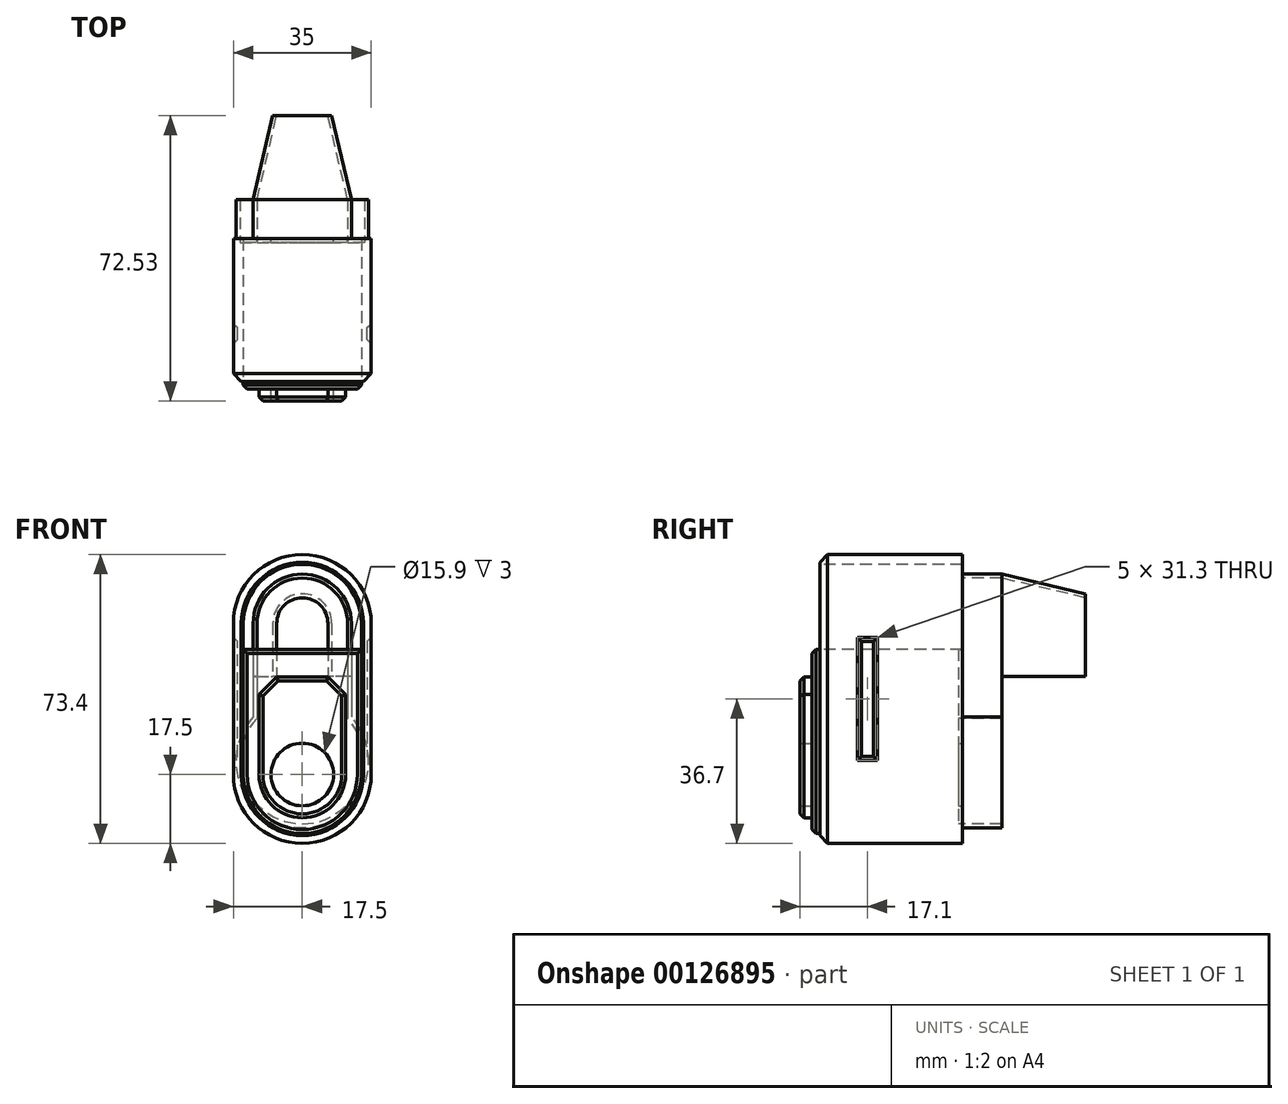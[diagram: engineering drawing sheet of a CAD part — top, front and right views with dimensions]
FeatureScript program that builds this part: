
annotation { "Feature Type Name" : "Feature", "Feature Type Description" : "" }
export const myFeature = defineFeature(function(context is Context, id is Id, definition is map)
    precondition{}
    {
        {
            var Q0;
            Q0=qCreatedBy(makeId("Front.planeOp"),FACE);
            var sketch = newSketch(context, id + "F0", { "sketchPlane" : qUnion([Q0])});
            skArc(sketch, "E0", {"start": v(-7.95, 0) * mm, "mid": v(-5.62, -5.62) * mm, "end": v(0, -7.95) * mm});
            skArc(sketch, "E1", {"start": v(-11, 0) * mm, "mid": v(0, -11) * mm, "end": v(11, 0) * mm});
            skArc(sketch, "E2", {"start": v(-15, 0) * mm, "mid": v(0, -15) * mm, "end": v(15, 0) * mm});
            skArc(sketch, "E3", {"start": v(-17.5, 0) * mm, "mid": v(0, -17.5) * mm, "end": v(17.5, 0) * mm});
            skLineSegment(sketch, "E4", {"start": v(0, -17.5) * mm, "end": v(0, 55.9) * mm, "construction": true});
            skLineSegment(sketch, "E5", {"start": v(-17.5, 0) * mm, "end": v(17.5, 0) * mm, "construction": true});
            skLineSegment(sketch, "E6", {"start": v(-17.5, -17.5) * mm, "end": v(-17.5, 55.9) * mm, "construction": true});
            skLineSegment(sketch, "E7", {"start": v(17.5, 55.9) * mm, "end": v(17.5, -17.5) * mm, "construction": true});
            skLineSegment(sketch, "E8", {"start": v(-17.5, -17.5) * mm, "end": v(17.5, -17.5) * mm, "construction": true});
            skLineSegment(sketch, "E9", {"start": v(-17.5, 55.9) * mm, "end": v(17.5, 55.9) * mm, "construction": true});
            skPoint(sketch, "E10.orphan", {"position": v(0, -30.99) * mm});
            skLineSegment(sketch, "E11", {"start": v(-17.5, 19.2) * mm, "end": v(17.5, 19.2) * mm, "construction": true});
            skArc(sketch, "E12.MirrorCS", {"start": v(7.95, 0) * mm, "mid": v(5.62, -5.62) * mm, "end": v(0, -7.95) * mm});
            skArc(sketch, "E13.MirrorCS", {"start": v(-15, 38.4) * mm, "mid": v(0, 53.4) * mm, "end": v(15, 38.4) * mm});
            skArc(sketch, "E14.MirrorCS", {"start": v(-17.5, 38.4) * mm, "mid": v(0, 55.9) * mm, "end": v(17.5, 38.4) * mm});
            skLineSegment(sketch, "E15", {"start": v(-17.5, 38.4) * mm, "end": v(-17.5, 0) * mm});
            skLineSegment(sketch, "E16", {"start": v(17.5, 38.4) * mm, "end": v(17.5, 0) * mm});
            skLineSegment(sketch, "E17", {"start": v(-15, 38.4) * mm, "end": v(-15, 0) * mm});
            skLineSegment(sketch, "E18", {"start": v(15, 38.4) * mm, "end": v(15, 0) * mm});
            skArc(sketch, "E19.MirrorCS", {"start": v(-7.95, 0) * mm, "mid": v(-5.62, 5.62) * mm, "end": v(0, 7.95) * mm});
            skArc(sketch, "E20.MirrorCS", {"start": v(7.95, 0) * mm, "mid": v(5.62, 5.62) * mm, "end": v(0, 7.95) * mm});
            skLineSegment(sketch, "E21", {"start": v(-17.5, 24.8) * mm, "end": v(17.5, 24.8) * mm, "construction": true});
            skLineSegment(sketch, "E22", {"start": v(-17.5, 31.8) * mm, "end": v(17.5, 31.8) * mm, "construction": true});
            skLineSegment(sketch, "E23", {"start": v(-11, 0) * mm, "end": v(-11, 24.8) * mm});
            skLineSegment(sketch, "E24", {"start": v(11, 0) * mm, "end": v(11, 24.8) * mm});
            skLineSegment(sketch, "E25", {"start": v(11, 24.8) * mm, "end": v(-11, 24.8) * mm});
            skLineSegment(sketch, "E26", {"start": v(-15, 31.8) * mm, "end": v(15, 31.8) * mm});
            skSolve(sketch);
        }
        {
            var Q0;
            Q0 = qSketchRegion(id + "F0", true);
            var Q1;
            Q1=makeQuery(id+"F0.imprint","IMPRINT",FACE,{"disambiguationData":[TD([[makeQuery(id+"F0.imprint","IMPRINT",EDGE,{"derivedFrom":sQuery(id+"F0.wireOp",EDGE,"E0")}),-1.0]])]});
            var Q2;
            Q2=makeQuery(id+"F0.imprint","IMPRINT",FACE,{"disambiguationData":[TD([[makeQuery(id+"F0.imprint","IMPRINT",EDGE,{"derivedFrom":sQuery(id+"F0.wireOp",EDGE,"E0")}),1.0]])]});
            var Q3;
            {var subQ0=sQuery(id+"F0.wireOp",EDGE,"E13.MirrorCS");Q3=makeQuery(id+"F0.imprint","IMPRINT",FACE,{"disambiguationData":[TD([[makeQuery(id+"F0.imprint","IMPRINT",EDGE,{"derivedFrom":subQ0}),-1.0]])]});}
            var Q4;
            Q4=makeQuery(id+"F0.imprint","IMPRINT",FACE,{"disambiguationData":[TD([[makeQuery(id+"F0.imprint","IMPRINT",EDGE,{"derivedFrom":sQuery(id+"F0.wireOp",EDGE,"E1")}),-1.0]])]});
            extrude(context, id + "F1", {"entities" : qUnion([Q0, Q1, Q2, Q3, Q4]), "oppositeDirection" : true, "depth" : 36.23 * mm});
        }
        {
            var Q0;
            Q0=makeQuery(id+"F0.imprint","IMPRINT",FACE,{"disambiguationData":[TD([[makeQuery(id+"F0.imprint","IMPRINT",EDGE,{"derivedFrom":sQuery(id+"F0.wireOp",EDGE,"E1")}),-1.0]])]});
            var Q1;
            Q1=makeQuery(id+"F0.imprint","IMPRINT",FACE,{"disambiguationData":[TD([[makeQuery(id+"F0.imprint","IMPRINT",EDGE,{"derivedFrom":sQuery(id+"F0.wireOp",EDGE,"E0")}),-1.0]])]});
            var Q2;
            Q2=makeQuery(id+"F0.imprint","IMPRINT",FACE,{"disambiguationData":[TD([[makeQuery(id+"F0.imprint","IMPRINT",EDGE,{"derivedFrom":sQuery(id+"F0.wireOp",EDGE,"E0")}),1.0]])]});
            extrude(context, id + "F2", {"entities" : qUnion([Q0, Q1, Q2]), "depth" : 2 * mm});
        }
        {
            var Q0;
            Q0=makeQuery(id+"F2.opExtrude","CAP_FACE",FACE,{"disambiguationData":[OSD([sQuery(id+"F0.wireOp",EDGE,"E2"),sQuery(id+"F0.wireOp",EDGE,"E17"),sQuery(id+"F0.wireOp",EDGE,"E18"),sQuery(id+"F0.wireOp",EDGE,"E26")])],"isStart":false});
            var sketch = newSketch(context, id + "F3", { "sketchPlane" : qUnion([Q0])});
            skLineSegment(sketch, "E27.0", {"start": v(-11, 0) * mm, "end": v(-11, 24.8) * mm});
            skLineSegment(sketch, "E28.0", {"start": v(11, 24.8) * mm, "end": v(-11, 24.8) * mm});
            skLineSegment(sketch, "E29.0", {"start": v(11, 0) * mm, "end": v(11, 24.8) * mm});
            skArc(sketch, "E30.0", {"start": v(-11, 0) * mm, "mid": v(0, -11) * mm, "end": v(11, 0) * mm});
            skArc(sketch, "E31.0", {"start": v(7.95, 0) * mm, "mid": v(5.62, -5.62) * mm, "end": v(0, -7.95) * mm});
            skArc(sketch, "E32.0", {"start": v(-7.95, 0) * mm, "mid": v(-5.62, -5.62) * mm, "end": v(0, -7.95) * mm});
            skArc(sketch, "E33.0", {"start": v(-7.95, 0) * mm, "mid": v(-5.62, 5.62) * mm, "end": v(0, 7.95) * mm});
            skArc(sketch, "E34.0", {"start": v(7.95, 0) * mm, "mid": v(5.62, 5.62) * mm, "end": v(0, 7.95) * mm});
            skSolve(sketch);
        }
        {
            var Q0;
            Q0 = qSketchRegion(id + "F3", true);
            var Q1;
            Q1=makeQuery(id+"F3.imprint","IMPRINT",FACE,{"disambiguationData":[TD([[makeQuery(id+"F3.imprint","IMPRINT",EDGE,{"derivedFrom":sQuery(id+"F3.wireOp",EDGE,"E31.0")}),-1.0]])]});
            extrude(context, id + "F4", {"entities" : qUnion([Q0, Q1]), "operationType" : NewBodyOperationType.ADD, "depth" : 3 * mm});
        }
        {
            var Q0;
            Q0=makeQuery(id+"F2.opExtrude","CAP_EDGE",EDGE,{"disambiguationData":[OSD([sQuery(id+"F0.wireOp",EDGE,"E26")])],"isStart":false});
            var Q1;
            Q1=makeQuery(id+"F2.opExtrude","CAP_EDGE",EDGE,{"disambiguationData":[OSD([sQuery(id+"F0.wireOp",EDGE,"E17")])],"isStart":false});
            chamfer(context, id + "F5", {"entities" : qUnion([Q0, Q1]), "width" : 1 * mm, "tangentPropagation" : true});
        }
        {
            var Q0;
            Q0=makeQuery(id+"F4.opExtrude","SWEPT_EDGE",EDGE,{"disambiguationData":[OSD([sQuery(id+"F3.wireOp",EDGE,"E28.0"),sQuery(id+"F3.wireOp",EDGE,"E29.0")])]});
            var Q1;
            Q1=makeQuery(id+"F4.opExtrude","SWEPT_EDGE",EDGE,{"disambiguationData":[OSD([sQuery(id+"F3.wireOp",EDGE,"E27.0"),sQuery(id+"F3.wireOp",EDGE,"E28.0")])]});
            chamfer(context, id + "F6", {"entities" : qUnion([Q0, Q1]), "width" : 4.4 * mm, "tangentPropagation" : true});
        }
        {
            var Q0;
            Q0=makeQuery(id+"F4.opExtrude","CAP_EDGE",EDGE,{"disambiguationData":[OSD([sQuery(id+"F3.wireOp",EDGE,"E27.0")])],"isStart":false});
            var Q1;
            Q1=makeQuery(id+"F4.opExtrude","CAP_EDGE",EDGE,{"disambiguationData":[OSD([sQuery(id+"F3.wireOp",EDGE,"E28.0")])],"isStart":false});
            var Q2;
            {var subQ0=sQuery(id+"F3.wireOp",EDGE,"E28.0");var subQ1=sQuery(id+"F3.wireOp",EDGE,"E27.0");Q2=makeQuery(id+"F6.opChamfer","BLEND_EDGE",EDGE,{"blendedFrom":[makeQuery(id+"F4.opExtrude","SWEPT_EDGE",EDGE,{"disambiguationData":[OSD([subQ1,subQ0])]}),makeQuery(id+"F4.opExtrude","CAP_FACE",FACE,{"disambiguationData":[OSD([subQ1,subQ0,sQuery(id+"F3.wireOp",EDGE,"E29.0"),sQuery(id+"F3.wireOp",EDGE,"E30.0")])],"isStart":false})],"blendedInto":[makeQuery(id+"F4.opExtrude","CAP_FACE",FACE,{"disambiguationData":[OSD([subQ1,subQ0,sQuery(id+"F3.wireOp",EDGE,"E29.0"),sQuery(id+"F3.wireOp",EDGE,"E30.0")])],"isStart":false})]});}
            var Q3;
            {var subQ0=sQuery(id+"F3.wireOp",EDGE,"E29.0");var subQ1=sQuery(id+"F3.wireOp",EDGE,"E28.0");Q3=makeQuery(id+"F6.opChamfer","BLEND_EDGE",EDGE,{"blendedFrom":[makeQuery(id+"F4.opExtrude","SWEPT_EDGE",EDGE,{"disambiguationData":[OSD([subQ1,subQ0])]}),makeQuery(id+"F4.opExtrude","CAP_FACE",FACE,{"disambiguationData":[OSD([sQuery(id+"F3.wireOp",EDGE,"E27.0"),subQ1,subQ0,sQuery(id+"F3.wireOp",EDGE,"E30.0")])],"isStart":false})],"blendedInto":[makeQuery(id+"F4.opExtrude","CAP_FACE",FACE,{"disambiguationData":[OSD([sQuery(id+"F3.wireOp",EDGE,"E27.0"),subQ1,subQ0,sQuery(id+"F3.wireOp",EDGE,"E30.0")])],"isStart":false})]});}
            chamfer(context, id + "F7", {"entities" : qUnion([Q0, Q1, Q2, Q3]), "width" : 1 * mm, "tangentPropagation" : true});
        }
        {
            var Q0;
            Q0=makeQuery(id+"F4.opExtrude","CAP_FACE",FACE,{"disambiguationData":[OSD([sQuery(id+"F3.wireOp",EDGE,"E27.0"),sQuery(id+"F3.wireOp",EDGE,"E28.0"),sQuery(id+"F3.wireOp",EDGE,"E29.0"),sQuery(id+"F3.wireOp",EDGE,"E30.0")])],"isStart":false});
            var sketch = newSketch(context, id + "F8", { "sketchPlane" : qUnion([Q0])});
            skArc(sketch, "E35.0", {"start": v(-7.95, 0) * mm, "mid": v(-5.62, 5.62) * mm, "end": v(0, 7.95) * mm});
            skArc(sketch, "E36.0", {"start": v(7.95, 0) * mm, "mid": v(5.62, 5.62) * mm, "end": v(0, 7.95) * mm});
            skArc(sketch, "E37.0", {"start": v(7.95, 0) * mm, "mid": v(5.62, -5.62) * mm, "end": v(0, -7.95) * mm});
            skArc(sketch, "E38.0", {"start": v(-7.95, 0) * mm, "mid": v(-5.62, -5.62) * mm, "end": v(0, -7.95) * mm});
            skArc(sketch, "E39.0", {"start": v(-7.45, 0) * mm, "mid": v(-5.27, 5.27) * mm, "end": v(0, 7.45) * mm});
            skArc(sketch, "E39.1", {"start": v(-7.45, 0) * mm, "mid": v(-5.27, -5.27) * mm, "end": v(0, -7.45) * mm});
            skArc(sketch, "E39.2", {"start": v(7.45, 0) * mm, "mid": v(5.27, -5.27) * mm, "end": v(0, -7.45) * mm});
            skArc(sketch, "E39.3", {"start": v(7.45, 0) * mm, "mid": v(5.27, 5.27) * mm, "end": v(0, 7.45) * mm});
            skCircle(sketch, "E40", {"center": v(0, 0) * mm, "radius": 0.75 * mm});
            skSolve(sketch);
        }
        {
            var Q0;
            Q0 = qSketchRegion(id + "F8", true);
            var Q1;
            Q1=makeQuery(id+"F8.imprint","IMPRINT",FACE,{"disambiguationData":[TD([[makeQuery(id+"F8.imprint","IMPRINT",EDGE,{"derivedFrom":sQuery(id+"F8.wireOp",EDGE,"E40")}),1.0]])]});
            extrude(context, id + "F9", {"entities" : qUnion([Q0, Q1]), "operationType" : NewBodyOperationType.REMOVE, "oppositeDirection" : true, "depth" : 1 * mm});
        }
        {
            var Q0;
            Q0=makeQuery(id+"F1.opExtrude","CAP_EDGE",EDGE,{"disambiguationData":[OSD([sQuery(id+"F0.wireOp",EDGE,"E15")])],"isStart":true});
            chamfer(context, id + "F10", {"entities" : qUnion([Q0]), "width" : 2 * mm, "tangentPropagation" : true});
        }
        {
            var Q0;
            Q0=makeQuery(id+"F1.opExtrude","SWEPT_FACE",FACE,{"disambiguationData":[OSD([sQuery(id+"F0.wireOp",EDGE,"E15")])]});
            var sketch = newSketch(context, id + "F11", { "sketchPlane" : qUnion([Q0])});
            skLineSegment(sketch, "E41", {"start": v(-25, 55.9) * mm, "end": v(-2, 55.9) * mm, "construction": true});
            skLineSegment(sketch, "E42", {"start": v(-2, -17.5) * mm, "end": v(-25, -17.5) * mm, "construction": true});
            skLineSegment(sketch, "E43.0", {"start": v(-2, 0) * mm, "end": v(-2, 38.4) * mm, "construction": true});
            skLineSegment(sketch, "E44", {"start": v(-36.23, 19.2) * mm, "end": v(-2, 19.2) * mm, "construction": true});
            skLineSegment(sketch, "E45.bottom", {"start": v(-9.6, 3.55) * mm, "end": v(-14.6, 3.55) * mm});
            skLineSegment(sketch, "E45.top", {"start": v(-9.6, 34.85) * mm, "end": v(-14.6, 34.85) * mm});
            skLineSegment(sketch, "E45.left", {"start": v(-9.6, 3.55) * mm, "end": v(-9.6, 34.85) * mm});
            skLineSegment(sketch, "E45.right", {"start": v(-14.6, 3.55) * mm, "end": v(-14.6, 34.85) * mm});
            skPoint(sketch, "E45.middle", {"position": v(-12.1, 19.2) * mm});
            skLineSegment(sketch, "E46.0", {"start": v(-2, 38.4) * mm, "end": v(-2, 55.9) * mm});
            skSolve(sketch);
        }
        {
            var Q0;
            Q0 = qSketchRegion(id + "F11", true);
            extrude(context, id + "F12", {"entities" : qUnion([Q0]), "operationType" : NewBodyOperationType.REMOVE, "oppositeDirection" : true, "depth" : 1 * mm});
        }
        {
            var Q0;
            Q0=makeQuery(id+"F1.opExtrude","SWEPT_FACE",FACE,{"disambiguationData":[OSD([sQuery(id+"F0.wireOp",EDGE,"E16")])]});
            var sketch = newSketch(context, id + "F13", { "sketchPlane" : qUnion([Q0])});
            skLineSegment(sketch, "E47.0", {"start": v(9.6, 34.85) * mm, "end": v(14.6, 34.85) * mm});
            skLineSegment(sketch, "E48.0", {"start": v(9.6, 3.55) * mm, "end": v(9.6, 34.85) * mm});
            skLineSegment(sketch, "E49.0", {"start": v(14.6, 3.55) * mm, "end": v(14.6, 34.85) * mm});
            skLineSegment(sketch, "E50.0", {"start": v(9.6, 3.55) * mm, "end": v(14.6, 3.55) * mm});
            skSolve(sketch);
        }
        {
            var Q0;
            Q0 = qSketchRegion(id + "F13", true);
            extrude(context, id + "F14", {"entities" : qUnion([Q0]), "operationType" : NewBodyOperationType.REMOVE, "oppositeDirection" : true, "depth" : 1 * mm});
        }
        {
            var Q0;
            Q0=makeQuery(id+"F14.boolean.opBoolean","COPY",EDGE,{"derivedFrom":makeQuery(id+"F14.opExtrude","CAP_EDGE",EDGE,{"disambiguationData":[OSD([sQuery(id+"F13.wireOp",EDGE,"E49.0")])],"isStart":false})});
            var Q1;
            Q1=makeQuery(id+"F14.boolean.opBoolean","COPY",EDGE,{"derivedFrom":makeQuery(id+"F14.opExtrude","CAP_EDGE",EDGE,{"disambiguationData":[OSD([sQuery(id+"F13.wireOp",EDGE,"E48.0")])],"isStart":false})});
            var Q2;
            Q2=makeQuery(id+"F14.boolean.opBoolean","COPY",EDGE,{"derivedFrom":makeQuery(id+"F14.opExtrude","CAP_EDGE",EDGE,{"disambiguationData":[OSD([sQuery(id+"F13.wireOp",EDGE,"E47.0")])],"isStart":false})});
            var Q3;
            Q3=makeQuery(id+"F14.boolean.opBoolean","COPY",EDGE,{"derivedFrom":makeQuery(id+"F14.opExtrude","CAP_EDGE",EDGE,{"disambiguationData":[OSD([sQuery(id+"F13.wireOp",EDGE,"E50.0")])],"isStart":false})});
            var Q4;
            Q4=makeQuery(id+"F12.boolean.opBoolean","COPY",FACE,{"derivedFrom":makeQuery(id+"F12.opExtrude","CAP_FACE",FACE,{"disambiguationData":[OSD([sQuery(id+"F11.wireOp",EDGE,"E45.bottom"),sQuery(id+"F11.wireOp",EDGE,"E45.top"),sQuery(id+"F11.wireOp",EDGE,"E45.left"),sQuery(id+"F11.wireOp",EDGE,"E45.right")])],"isStart":false})});
            chamfer(context, id + "F15", {"entities" : qUnion([Q0, Q1, Q2, Q3, Q4]), "width" : 1 * mm, "tangentPropagation" : true});
        }
        {
            var Q0;
            Q0=makeQuery(id+"F1.opExtrude","CAP_FACE",FACE,{"disambiguationData":[OSD([sQuery(id+"F0.wireOp",EDGE,"E3"),sQuery(id+"F0.wireOp",EDGE,"E14.MirrorCS"),sQuery(id+"F0.wireOp",EDGE,"E15"),sQuery(id+"F0.wireOp",EDGE,"E16")])],"isStart":false});
            var sketch = newSketch(context, id + "F16", { "sketchPlane" : qUnion([Q0])});
            skLineSegment(sketch, "E51.0", {"start": v(-17.5, 38.4) * mm, "end": v(-17.5, 0) * mm, "construction": true});
            skArc(sketch, "E52.0", {"start": v(17.5, 38.4) * mm, "mid": v(0, 55.9) * mm, "end": v(-17.5, 38.4) * mm, "construction": true});
            skLineSegment(sketch, "E53.0", {"start": v(17.5, 38.4) * mm, "end": v(17.5, 0) * mm, "construction": true});
            skArc(sketch, "E54.0", {"start": v(17.5, 0) * mm, "mid": v(0, -17.5) * mm, "end": v(-17.5, 0) * mm, "construction": true});
            skLineSegment(sketch, "E55.0", {"start": v(-12.5, 38.4) * mm, "end": v(-12.5, 14.65) * mm});
            skArc(sketch, "E55.1", {"start": v(12.5, 38.4) * mm, "mid": v(0, 50.9) * mm, "end": v(-12.5, 38.4) * mm});
            skLineSegment(sketch, "E55.2", {"start": v(12.5, 38.4) * mm, "end": v(12.5, 14.65) * mm});
            skArc(sketch, "E56.0", {"start": v(11.5, 38.4) * mm, "mid": v(0, 49.9) * mm, "end": v(-11.5, 38.4) * mm});
            skLineSegment(sketch, "E56.1", {"start": v(11.5, 38.4) * mm, "end": v(11.5, 14.26) * mm});
            skLineSegment(sketch, "E56.3", {"start": v(-11.5, 38.4) * mm, "end": v(-11.5, 14.26) * mm});
            skLineSegment(sketch, "E57.0", {"start": v(17.5, 19.2) * mm, "end": v(-17.5, 19.2) * mm, "construction": true});
            skLineSegment(sketch, "E58.0", {"start": v(-11, 24.8) * mm, "end": v(11, 24.8) * mm, "construction": true});
            skLineSegment(sketch, "E59.0", {"start": v(15, 31.8) * mm, "end": v(-15, 31.8) * mm, "construction": true});
            skLineSegment(sketch, "E60.0", {"start": v(0, -17.5) * mm, "end": v(0, 55.9) * mm, "construction": true});
            skLineSegment(sketch, "E61", {"start": v(-17.5, 3.35) * mm, "end": v(17.5, 3.35) * mm, "construction": true});
            skPoint(sketch, "E62", {"position": v(0, -12.5) * mm});
            skArc(sketch, "E63", {"start": v(-11.5, 14.26) * mm, "mid": v(0, -12.5) * mm, "end": v(11.5, 14.26) * mm});
            skArc(sketch, "E64.0", {"start": v(-12.5, 14.65) * mm, "mid": v(0, -13.5) * mm, "end": v(12.5, 14.65) * mm});
            skArc(sketch, "E65.0", {"start": v(7.95, 0) * mm, "mid": v(5.62, -5.62) * mm, "end": v(0, -7.95) * mm});
            skArc(sketch, "E66.0", {"start": v(7.95, 0) * mm, "mid": v(5.62, 5.62) * mm, "end": v(0, 7.95) * mm});
            skArc(sketch, "E67.0", {"start": v(-7.95, 0) * mm, "mid": v(-5.62, 5.62) * mm, "end": v(0, 7.95) * mm});
            skArc(sketch, "E68.0", {"start": v(-7.95, 0) * mm, "mid": v(-5.62, -5.62) * mm, "end": v(0, -7.95) * mm});
            skSolve(sketch);
        }
        {
            var Q0;
            Q0 = qSketchRegion(id + "F16", true);
            extrude(context, id + "F17", {"entities" : qUnion([Q0]), "operationType" : NewBodyOperationType.ADD, "depth" : 10 * mm});
        }
        {
            var Q0;
            Q0=makeQuery(id+"F16.imprint","IMPRINT",FACE,{"disambiguationData":[TD([[makeQuery(id+"F16.imprint","IMPRINT",EDGE,{"derivedFrom":sQuery(id+"F16.wireOp",EDGE,"E65.0")}),-1.0]])]});
            extrude(context, id + "F18", {"entities" : qUnion([Q0]), "operationType" : NewBodyOperationType.REMOVE, "oppositeDirection" : true, "depth" : 1 * mm});
        }
        {
            var Q0;
            Q0=makeQuery(id+"F17.opExtrude","CAP_FACE",FACE,{"disambiguationData":[OSD([sQuery(id+"F16.wireOp",EDGE,"E55.0"),sQuery(id+"F16.wireOp",EDGE,"E55.1"),sQuery(id+"F16.wireOp",EDGE,"E55.2"),sQuery(id+"F16.wireOp",EDGE,"E56.0"),sQuery(id+"F16.wireOp",EDGE,"E56.1"),sQuery(id+"F16.wireOp",EDGE,"E56.3"),sQuery(id+"F16.wireOp",EDGE,"E63"),sQuery(id+"F16.wireOp",EDGE,"E64.0")])],"isStart":false});
            var sketch = newSketch(context, id + "F19", { "sketchPlane" : qUnion([Q0])});
            skArc(sketch, "E69.0", {"start": v(12.5, 38.4) * mm, "mid": v(0, 50.9) * mm, "end": v(-12.5, 38.4) * mm});
            skArc(sketch, "E70.0", {"start": v(11.5, 38.4) * mm, "mid": v(0, 49.9) * mm, "end": v(-11.5, 38.4) * mm});
            skLineSegment(sketch, "E71.0", {"start": v(-11.5, 38.4) * mm, "end": v(-11.5, 14.26) * mm});
            skLineSegment(sketch, "E72.0", {"start": v(-12.5, 38.4) * mm, "end": v(-12.5, 14.65) * mm});
            skLineSegment(sketch, "E73.0", {"start": v(11.5, 38.4) * mm, "end": v(11.5, 14.26) * mm});
            skLineSegment(sketch, "E74.0", {"start": v(12.5, 38.4) * mm, "end": v(12.5, 14.65) * mm});
            skPoint(sketch, "E75", {"position": v(0, 50.9) * mm});
            skPoint(sketch, "E76", {"position": v(0, 13.94) * mm});
            skPoint(sketch, "E77.orphan", {"position": v(-12.5, 14.65) * mm});
            skPoint(sketch, "E78.orphan", {"position": v(-11.5, 14.26) * mm});
            skPoint(sketch, "E79.orphan", {"position": v(11.5, 14.26) * mm});
            skPoint(sketch, "E80.orphan", {"position": v(12.5, 14.65) * mm});
            skLineSegment(sketch, "E81.0", {"start": v(-6.5, 38.4) * mm, "end": v(-6.5, 13.94) * mm});
            skArc(sketch, "E81.1", {"start": v(6.5, 38.4) * mm, "mid": v(0, 44.9) * mm, "end": v(-6.5, 38.4) * mm, "construction": true});
            skLineSegment(sketch, "E81.2", {"start": v(6.5, 38.4) * mm, "end": v(6.5, 13.94) * mm, "construction": true});
            skLineSegment(sketch, "E82.0", {"start": v(-7.5, 38.4) * mm, "end": v(-7.5, 13.94) * mm, "construction": true});
            skArc(sketch, "E82.1", {"start": v(7.5, 38.4) * mm, "mid": v(0, 45.9) * mm, "end": v(-7.5, 38.4) * mm, "construction": true});
            skLineSegment(sketch, "E82.2", {"start": v(7.5, 38.4) * mm, "end": v(7.5, 13.94) * mm, "construction": true});
            skLineSegment(sketch, "E83", {"start": v(-11.5, 13.94) * mm, "end": v(11.5, 13.94) * mm, "construction": true});
            skLineSegment(sketch, "E84", {"start": v(-12.5, 14.65) * mm, "end": v(-11.5, 14.65) * mm});
            skLineSegment(sketch, "E85", {"start": v(12.5, 14.65) * mm, "end": v(11.5, 14.65) * mm});
            skPoint(sketch, "E86.start.orphan", {"position": v(-12.5, 13.94) * mm});
            skLineSegment(sketch, "E87", {"start": v(-12.5, 24.96) * mm, "end": v(12.5, 24.96) * mm, "construction": true});
            skLineSegment(sketch, "E88", {"start": v(-12.5, 24.96) * mm, "end": v(-11.5, 24.96) * mm});
            skLineSegment(sketch, "E89", {"start": v(11.5, 24.96) * mm, "end": v(12.5, 24.96) * mm});
            skSolve(sketch);
        }
        {
            var Q0;
            Q0=makeQuery(id+"F19.imprint","IMPRINT",FACE,{"disambiguationData":[TD([[makeQuery(id+"F19.imprint","IMPRINT",EDGE,{"derivedFrom":sQuery(id+"F19.wireOp",EDGE,"E69.0")}),1.0]])]});
            cPlane(context, id + "F20", {"entities" : qUnion([Q0]), "cplaneType" : CPlaneType.OFFSET, "offset" : 21.3 * mm, "width" : 150 * mm, "height" : 150 * mm});
        }
        {
            var Q0;
            Q0=qCreatedBy(id+"F20.planeOp",FACE);
            var sketch = newSketch(context, id + "F21", { "sketchPlane" : qUnion([Q0])});
            skLineSegment(sketch, "E90.0", {"start": v(-7.5, 38.4) * mm, "end": v(-7.5, 13.94) * mm});
            skLineSegment(sketch, "E91.0", {"start": v(-6.5, 38.4) * mm, "end": v(-6.5, 13.94) * mm});
            skLineSegment(sketch, "E92.0", {"start": v(6.5, 38.4) * mm, "end": v(6.5, 13.94) * mm});
            skLineSegment(sketch, "E93.0", {"start": v(7.5, 38.4) * mm, "end": v(7.5, 13.94) * mm});
            skArc(sketch, "E94.0", {"start": v(6.5, 38.4) * mm, "mid": v(0, 44.9) * mm, "end": v(-6.5, 38.4) * mm});
            skArc(sketch, "E95.0", {"start": v(7.5, 38.4) * mm, "mid": v(0, 45.9) * mm, "end": v(-7.5, 38.4) * mm});
            skLineSegment(sketch, "E96", {"start": v(-7.5, 13.94) * mm, "end": v(-6.5, 13.94) * mm});
            skLineSegment(sketch, "E97", {"start": v(6.5, 13.94) * mm, "end": v(7.5, 13.94) * mm});
            skLineSegment(sketch, "E98.0", {"start": v(-12.5, 24.96) * mm, "end": v(12.5, 24.96) * mm, "construction": true});
            skLineSegment(sketch, "E99", {"start": v(-7.5, 24.96) * mm, "end": v(-6.5, 24.96) * mm, "construction": true});
            skLineSegment(sketch, "E100", {"start": v(-7.5, 24.96) * mm, "end": v(-6.5, 24.96) * mm});
            skLineSegment(sketch, "E101", {"start": v(6.5, 24.96) * mm, "end": v(7.5, 24.96) * mm});
            skSolve(sketch);
        }
        {
            var Q1;
            {var subQ1=sQuery(id+"F19.wireOp",EDGE,"E69.0");Q1=makeQuery(id+"F19.imprint","IMPRINT",FACE,{"disambiguationData":[TD([[makeQuery(id+"F19.imprint","IMPRINT",EDGE,{"derivedFrom":subQ1}),1.0]])]});}
            var Q2;
            {var subQ3=sQuery(id+"F21.wireOp",EDGE,"E94.0");Q2=makeQuery(id+"F21.imprint","IMPRINT",FACE,{"disambiguationData":[TD([[makeQuery(id+"F21.imprint","IMPRINT",EDGE,{"derivedFrom":subQ3}),-1.0]])]});}
            loft(context, id + "F22", {"operationType" : NewBodyOperationType.ADD, "sheetProfilesArray" : [{ "sheetProfileEntities" : qUnion([Q1]) }, { "sheetProfileEntities" : qUnion([Q2]) }]});
        }
    });
